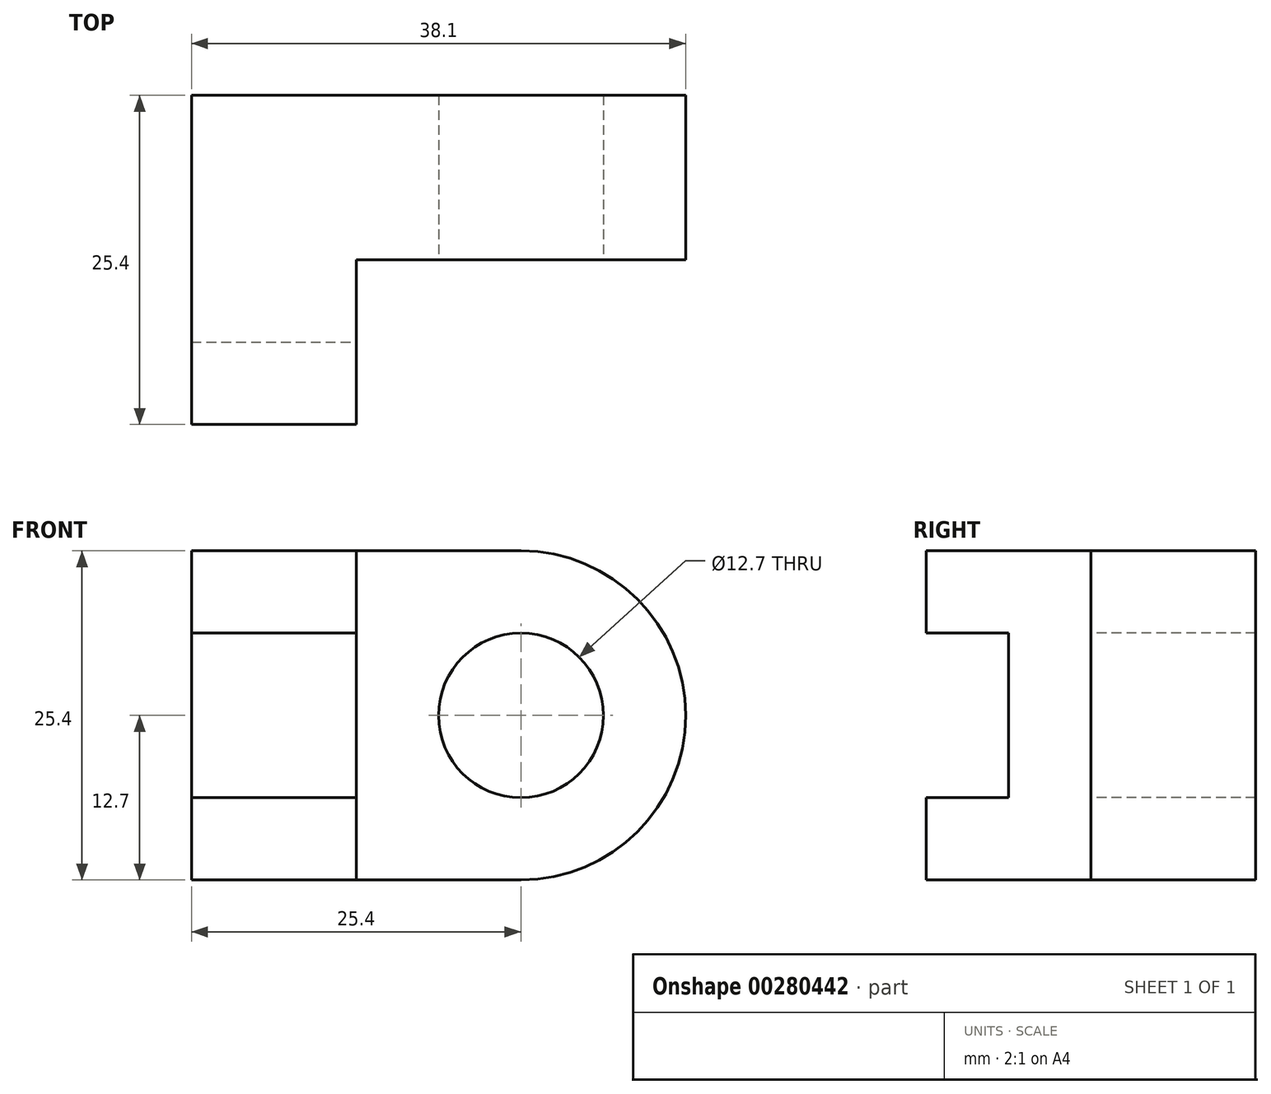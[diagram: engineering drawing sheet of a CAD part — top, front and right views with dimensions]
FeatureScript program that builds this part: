
annotation { "Feature Type Name" : "Feature", "Feature Type Description" : "" }
export const myFeature = defineFeature(function(context is Context, id is Id, definition is map)
    precondition{}
    {
        {
            var Q0;
            Q0=qCreatedBy(makeId("Front.planeOp"),FACE);
            var sketch = newSketch(context, id + "F0", { "sketchPlane" : qUnion([Q0])});
            skLineSegment(sketch, "E0", {"start": v(-12.7, 0) * mm, "end": v(0, 0) * mm});
            skLineSegment(sketch, "E1", {"start": v(0, 0) * mm, "end": v(12.7, 0) * mm});
            skLineSegment(sketch, "E2", {"start": v(12.7, 0) * mm, "end": v(-12.7, 0) * mm});
            skLineSegment(sketch, "E3", {"start": v(-12.7, 0) * mm, "end": v(-12.7, 25.4) * mm});
            skLineSegment(sketch, "E4", {"start": v(-12.7, 25.4) * mm, "end": v(0, 25.4) * mm});
            skLineSegment(sketch, "E5", {"start": v(0, 25.4) * mm, "end": v(12.7, 25.4) * mm});
            skArc(sketch, "E6", {"start": v(12.7, 0) * mm, "mid": v(25.4, 12.7) * mm, "end": v(12.7, 25.4) * mm});
            skSolve(sketch);
        }
        {
            var Q0;
            Q0 = qSketchRegion(id + "F0", true);
            extrude(context, id + "F1", {"entities" : qUnion([Q0]), "oppositeDirection" : true, "depth" : 25.4 * mm});
        }
        {
            var Q0;
            Q0=qCreatedBy(makeId("Front.planeOp"),FACE);
            var sketch = newSketch(context, id + "F2", { "sketchPlane" : qUnion([Q0])});
            skLineSegment(sketch, "E7.bottom", {"start": v(0, 25.4) * mm, "end": v(25.4, 25.4) * mm});
            skLineSegment(sketch, "E7.top", {"start": v(0, 0) * mm, "end": v(25.4, 0) * mm});
            skLineSegment(sketch, "E7.left", {"start": v(0, 25.4) * mm, "end": v(0, 0) * mm});
            skLineSegment(sketch, "E7.right", {"start": v(25.4, 25.4) * mm, "end": v(25.4, 0) * mm});
            skSolve(sketch);
        }
        {
            var Q0;
            Q0=qCreatedBy(makeId("Front.planeOp"),FACE);
            var sketch = newSketch(context, id + "F3", { "sketchPlane" : qUnion([Q0])});
            skLineSegment(sketch, "E8.bottom", {"start": v(-12.7, 19.05) * mm, "end": v(0, 19.05) * mm});
            skLineSegment(sketch, "E8.top", {"start": v(-12.7, 6.35) * mm, "end": v(0, 6.35) * mm});
            skLineSegment(sketch, "E8.left", {"start": v(-12.7, 19.05) * mm, "end": v(-12.7, 6.35) * mm});
            skLineSegment(sketch, "E8.right", {"start": v(0, 19.05) * mm, "end": v(0, 6.35) * mm});
            skSolve(sketch);
        }
        {
            var Q0;
            Q0=qCreatedBy(makeId("Front.planeOp"),FACE);
            var sketch = newSketch(context, id + "F4", { "sketchPlane" : qUnion([Q0])});
            skCircle(sketch, "E9", {"center": v(12.7, 12.7) * mm, "radius": 6.35 * mm});
            skSolve(sketch);
        }
        {
            var Q0;
            Q0 = qSketchRegion(id + "F2", true);
            extrude(context, id + "F5", {"entities" : qUnion([Q0]), "operationType" : NewBodyOperationType.REMOVE, "oppositeDirection" : true, "depth" : 12.7 * mm});
        }
        {
            var Q0;
            Q0 = qSketchRegion(id + "F3", true);
            extrude(context, id + "F6", {"entities" : qUnion([Q0]), "operationType" : NewBodyOperationType.REMOVE, "oppositeDirection" : true, "depth" : 6.35 * mm});
        }
        {
            var Q0;
            Q0 = qSketchRegion(id + "F4", true);
            extrude(context, id + "F7", {"entities" : qUnion([Q0]), "operationType" : NewBodyOperationType.REMOVE, "oppositeDirection" : true, "depth" : 25.4 * mm});
        }
    });
